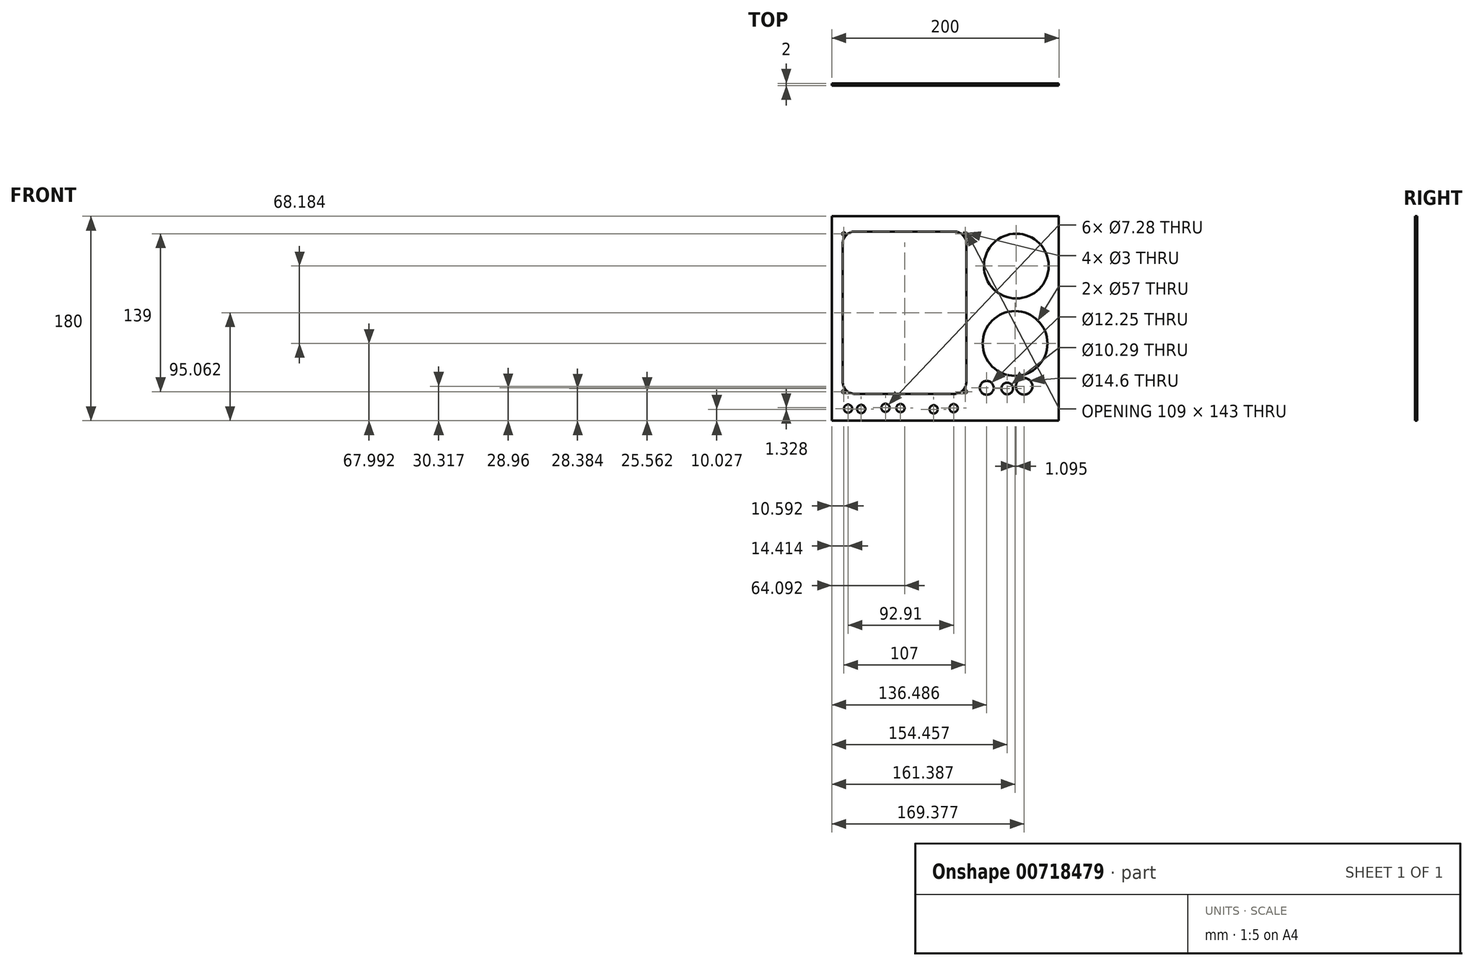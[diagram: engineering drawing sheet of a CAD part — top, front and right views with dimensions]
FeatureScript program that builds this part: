
annotation { "Feature Type Name" : "Feature", "Feature Type Description" : "" }
export const myFeature = defineFeature(function(context is Context, id is Id, definition is map)
    precondition{}
    {
        {
            var Q0;
            Q0=qCreatedBy(makeId("Front.planeOp"),FACE);
            var sketch = newSketch(context, id + "F0", { "sketchPlane" : qUnion([Q0])});
            skLineSegment(sketch, "E0.bottom", {"start": v(-80.55, 71.9) * mm, "end": v(119.45, 71.9) * mm});
            skLineSegment(sketch, "E0.top", {"start": v(-80.55, -108.1) * mm, "end": v(119.45, -108.1) * mm});
            skLineSegment(sketch, "E0.left", {"start": v(-80.55, 71.9) * mm, "end": v(-80.55, -108.1) * mm});
            skLineSegment(sketch, "E0.right", {"start": v(119.45, 71.9) * mm, "end": v(119.45, -108.1) * mm});
            skLineSegment(sketch, "E1.bottom", {"start": v(-60.1, 58.46) * mm, "end": v(27.2, 58.46) * mm});
            skLineSegment(sketch, "E1.top", {"start": v(-60.1, -84.54) * mm, "end": v(27.2, -84.54) * mm});
            skLineSegment(sketch, "E1.left", {"start": v(-70.96, 47.61) * mm, "end": v(-70.96, -73.69) * mm});
            skLineSegment(sketch, "E1.right", {"start": v(38.04, 47.61) * mm, "end": v(38.04, -73.69) * mm});
            skCircle(sketch, "E2", {"center": v(81.93, 28.08) * mm, "radius": 28.5 * mm});
            skCircle(sketch, "E3", {"center": v(80.84, -40.1) * mm, "radius": 28.5 * mm});
            skCircle(sketch, "E4", {"center": v(55.94, -79.14) * mm, "radius": 6.12 * mm});
            skCircle(sketch, "E5", {"center": v(73.9, -79.72) * mm, "radius": 5.15 * mm});
            skCircle(sketch, "E6", {"center": v(88.83, -77.78) * mm, "radius": 7.3 * mm});
            skCircle(sketch, "E7", {"center": v(-66.14, -97.42) * mm, "radius": 3.64 * mm});
            skCircle(sketch, "E8", {"center": v(-54.6, -97.83) * mm, "radius": 3.64 * mm});
            skCircle(sketch, "E9", {"center": v(-33.24, -96.75) * mm, "radius": 3.64 * mm});
            skCircle(sketch, "E10", {"center": v(-20.02, -97) * mm, "radius": 3.64 * mm});
            skCircle(sketch, "E11", {"center": v(9.14, -98.07) * mm, "radius": 3.64 * mm});
            skCircle(sketch, "E12", {"center": v(26.77, -97.05) * mm, "radius": 3.64 * mm});
            skPoint(sketch, "E13.visualSharp", {"position": v(-70.96, 58.46) * mm});
            skArc(sketch, "E13.filletArc", {"start": v(-60.1, 58.46) * mm, "mid": v(-67.78, 55.28) * mm, "end": v(-70.96, 47.61) * mm});
            skPoint(sketch, "E14.visualSharp", {"position": v(-70.96, -84.54) * mm});
            skArc(sketch, "E14.filletArc", {"start": v(-70.96, -73.69) * mm, "mid": v(-67.78, -81.36) * mm, "end": v(-60.1, -84.54) * mm});
            skPoint(sketch, "E15.visualSharp", {"position": v(38.04, -84.54) * mm});
            skArc(sketch, "E15.filletArc", {"start": v(27.2, -84.54) * mm, "mid": v(34.86, -81.36) * mm, "end": v(38.04, -73.69) * mm});
            skPoint(sketch, "E16.visualSharp", {"position": v(38.04, 58.46) * mm});
            skArc(sketch, "E16.filletArc", {"start": v(38.04, 47.61) * mm, "mid": v(34.86, 55.28) * mm, "end": v(27.2, 58.46) * mm});
            skLineSegment(sketch, "E17", {"start": v(-16.46, 58.46) * mm, "end": v(-16.46, -84.54) * mm, "construction": true});
            skLineSegment(sketch, "E18", {"start": v(38.04, -13.04) * mm, "end": v(-70.96, -13.04) * mm, "construction": true});
            skCircle(sketch, "E19", {"center": v(37.04, 56.46) * mm, "radius": 1.5 * mm});
            skCircle(sketch, "E20", {"center": v(37.04, -82.54) * mm, "radius": 1.5 * mm});
            skCircle(sketch, "E21", {"center": v(-69.96, -82.54) * mm, "radius": 1.5 * mm});
            skCircle(sketch, "E22", {"center": v(-69.96, 56.46) * mm, "radius": 1.5 * mm});
            skSolve(sketch);
        }
        {
            var Q0;
            Q0=makeQuery(id+"F0.imprint","IMPRINT",FACE,{"disambiguationData":[TD([[makeQuery(id+"F0.imprint","IMPRINT",EDGE,{"derivedFrom":sQuery(id+"F0.wireOp",EDGE,"E0.bottom")}),-1.0]])]});
            extrude(context, id + "F1", {"entities" : qUnion([Q0]), "depth" : 2 * mm, "offsetDistance" : 25 * mm});
        }
    });
